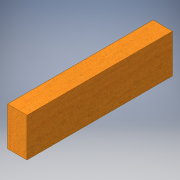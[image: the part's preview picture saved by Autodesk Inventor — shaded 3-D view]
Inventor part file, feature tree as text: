
AUTODESK INVENTOR PART (.ipt)
format: ipt  version: 2016 (Build 200138000, 138)  size: 108,032 bytes
history: native  units: in
note: dims shown in document units (in); Inventor stores cm internally (conversion verified against a paired STEP export)
features: extrude x1, sketch x1
ambient origin geometry x8: Origin, YZ Plane, XZ Plane, XY Plane, X Axis, Y Axis, Z Axis, Center Point
bodies: Solid1 (feature_tree)
feature tree (2):
  extrude  "Extrusion1"  Depth=4.0in
  sketch  "Sketch1"  dims[d0=2.0in d1=4.0in d2=15.0in d3=0.0in]
